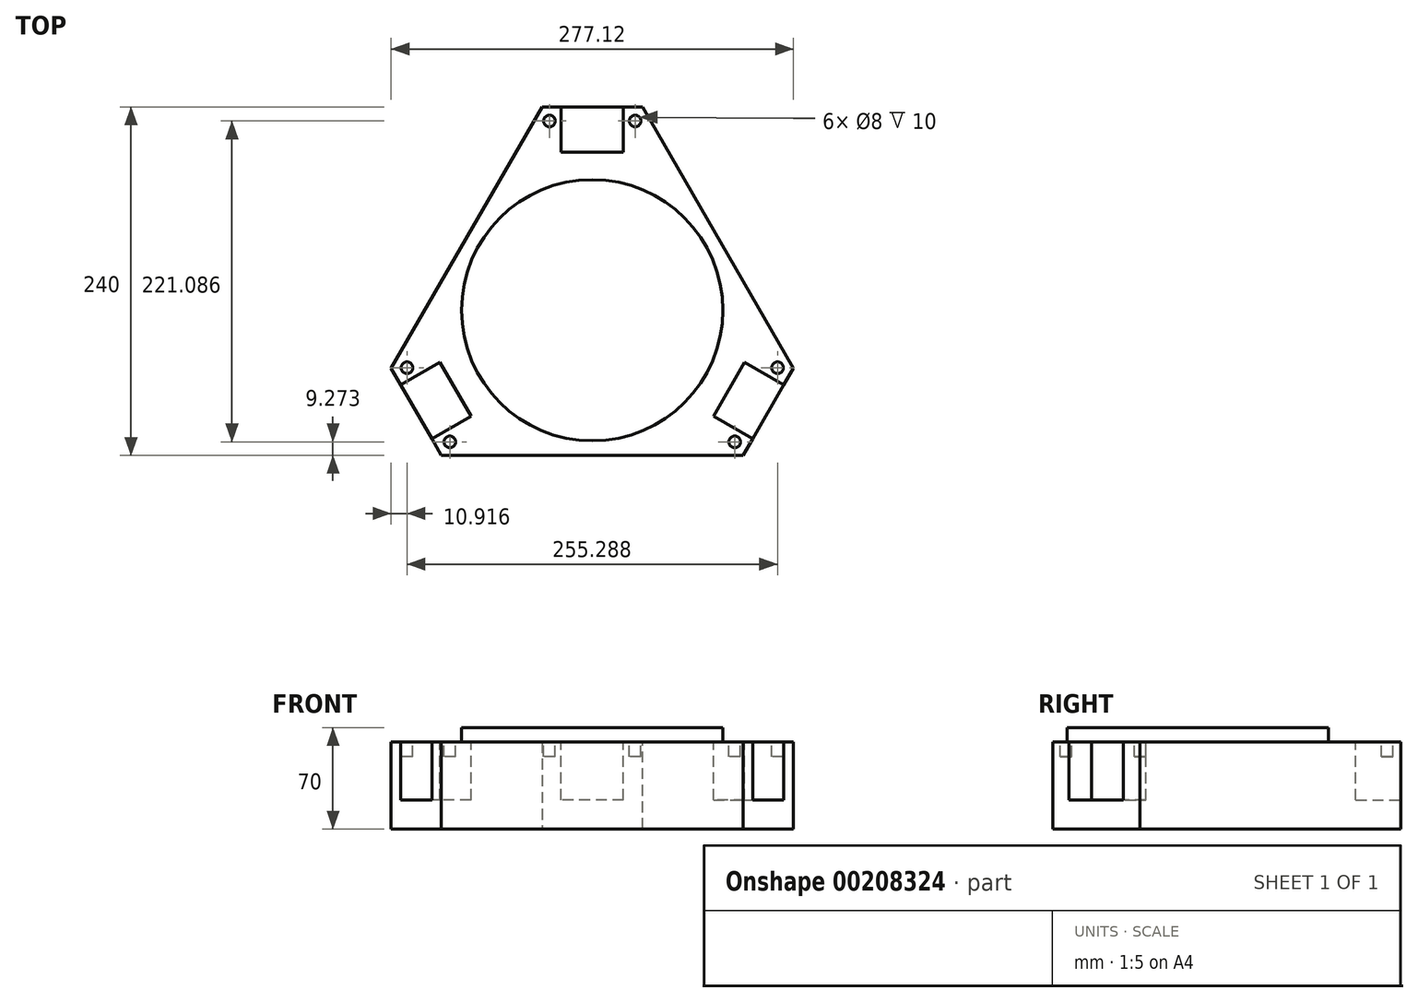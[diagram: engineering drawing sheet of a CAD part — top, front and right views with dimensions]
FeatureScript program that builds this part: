
annotation { "Feature Type Name" : "Feature", "Feature Type Description" : "" }
export const myFeature = defineFeature(function(context is Context, id is Id, definition is map)
    precondition{}
    {
        {
            var Q0;
            Q0=qCreatedBy(makeId("Top.planeOp"),FACE);
            var sketch = newSketch(context, id + "F0", { "sketchPlane" : qUnion([Q0])});
            skCircle(sketch, "E0.cCircle", {"center": v(0, 0) * mm, "radius": 100 * mm, "construction": true});
            skLineSegment(sketch, "E0.0", {"start": v(173.2, -100) * mm, "end": v(-173.2, -100) * mm});
            skLineSegment(sketch, "E0.1", {"start": v(-173.2, -100) * mm, "end": v(0, 200) * mm});
            skLineSegment(sketch, "E0.2", {"start": v(0, 200) * mm, "end": v(173.2, -100) * mm});
            skPoint(sketch, "E0.0.midPoint", {"position": v(0, -100) * mm});
            skSolve(sketch);
        }
        {
            var Q0;
            Q0=qSketchRegion(id+"F0",true);
            extrude(context, id + "F1", {"entities" : qUnion([Q0]), "depth" : 60 * mm});
        }
        {
            var Q0;
            Q0=makeQuery(id+"F1.opExtrude","SWEPT_EDGE",EDGE,{"disambiguationData":[OSD([sQuery(id+"F0.wireOp",EDGE,"E0.0"),sQuery(id+"F0.wireOp",EDGE,"E0.1")])]});
            var Q1;
            Q1=makeQuery(id+"F1.opExtrude","SWEPT_EDGE",EDGE,{"disambiguationData":[OSD([sQuery(id+"F0.wireOp",EDGE,"E0.0"),sQuery(id+"F0.wireOp",EDGE,"E0.2")])]});
            var Q2;
            Q2=makeQuery(id+"F1.opExtrude","SWEPT_EDGE",EDGE,{"disambiguationData":[OSD([sQuery(id+"F0.wireOp",EDGE,"E0.1"),sQuery(id+"F0.wireOp",EDGE,"E0.2")])]});
            chamfer(context, id + "F2", {"entities" : qUnion([Q0, Q1, Q2]), "width" : 40 * mm, "tangentPropagation" : true});
        }
        {
            var Q0;
            Q0=makeQuery(id+"F1.opExtrude","CAP_FACE",FACE,{"disambiguationData":[OSD([sQuery(id+"F0.wireOp",EDGE,"E0.0"),sQuery(id+"F0.wireOp",EDGE,"E0.1"),sQuery(id+"F0.wireOp",EDGE,"E0.2")])],"isStart":false});
            var sketch = newSketch(context, id + "F3", { "sketchPlane" : qUnion([Q0])});
            skCircle(sketch, "E1", {"center": v(0, 0) * mm, "radius": 90 * mm});
            skSolve(sketch);
        }
        {
            var Q0;
            Q0=qSketchRegion(id+"F3",true);
            extrude(context, id + "F4", {"entities" : qUnion([Q0]), "operationType" : NewBodyOperationType.ADD, "depth" : 10 * mm});
        }
        {
            var Q0;
            Q0=makeQuery(id+"F1.opExtrude","CAP_FACE",FACE,{"disambiguationData":[OSD([sQuery(id+"F0.wireOp",EDGE,"E0.0"),sQuery(id+"F0.wireOp",EDGE,"E0.1"),sQuery(id+"F0.wireOp",EDGE,"E0.2")])],"isStart":false});
            var sketch = newSketch(context, id + "F5", { "sketchPlane" : qUnion([Q0])});
            skLineSegment(sketch, "E2.bottom", {"start": v(-21.5, 108.86) * mm, "end": v(21.5, 108.86) * mm});
            skLineSegment(sketch, "E2.top", {"start": v(-21.5, 151.86) * mm, "end": v(21.5, 151.86) * mm});
            skLineSegment(sketch, "E2.left", {"start": v(-21.5, 108.86) * mm, "end": v(-21.5, 151.86) * mm});
            skLineSegment(sketch, "E2.right", {"start": v(21.5, 108.86) * mm, "end": v(21.5, 151.86) * mm});
            skPoint(sketch, "E2.middle", {"position": v(0, 130.36) * mm});
            skLineSegment(sketch, "E3.1.0", {"start": v(-83.52, -73.05) * mm, "end": v(-105.02, -35.8) * mm});
            skPoint(sketch, "E3.1.1", {"position": v(-112.9, -65.18) * mm});
            skLineSegment(sketch, "E3.1.2", {"start": v(-105.02, -35.8) * mm, "end": v(-142.26, -57.3) * mm});
            skLineSegment(sketch, "E3.1.3", {"start": v(-83.52, -73.05) * mm, "end": v(-120.76, -94.55) * mm});
            skLineSegment(sketch, "E3.1.4", {"start": v(-120.76, -94.55) * mm, "end": v(-142.26, -57.3) * mm});
            skLineSegment(sketch, "E3.2.0", {"start": v(105.02, -35.8) * mm, "end": v(83.52, -73.05) * mm});
            skPoint(sketch, "E3.2.1", {"position": v(112.9, -65.18) * mm});
            skLineSegment(sketch, "E3.2.2", {"start": v(83.52, -73.05) * mm, "end": v(120.76, -94.55) * mm});
            skLineSegment(sketch, "E3.2.3", {"start": v(105.02, -35.8) * mm, "end": v(142.26, -57.3) * mm});
            skLineSegment(sketch, "E3.2.4", {"start": v(142.26, -57.3) * mm, "end": v(120.76, -94.55) * mm});
            skPoint(sketch, "E3.center", {"position": v(0, 0) * mm});
            skSolve(sketch);
        }
        {
            var Q0;
            Q0=qSketchRegion(id+"F5",true);
            extrude(context, id + "F6", {"entities" : qUnion([Q0]), "operationType" : NewBodyOperationType.REMOVE, "oppositeDirection" : true, "depth" : 40 * mm});
        }
        {
            var Q0;
            Q0=makeQuery(id+"F1.opExtrude","CAP_FACE",FACE,{"disambiguationData":[OSD([sQuery(id+"F0.wireOp",EDGE,"E0.0"),sQuery(id+"F0.wireOp",EDGE,"E0.1"),sQuery(id+"F0.wireOp",EDGE,"E0.2")])],"isStart":false});
            var sketch = newSketch(context, id + "F7", { "sketchPlane" : qUnion([Q0])});
            skCircle(sketch, "E4", {"center": v(-29.5, 130.36) * mm, "radius": 4 * mm});
            skPoint(sketch, "E4.centerSnap0", {"position": v(-21.5, 130.36) * mm});
            skCircle(sketch, "E5", {"center": v(29.5, 130.36) * mm, "radius": 4 * mm});
            skPoint(sketch, "E5.centerSnap0", {"position": v(21.5, 130.36) * mm});
            skCircle(sketch, "E6.1.0", {"center": v(-98.14, -90.73) * mm, "radius": 4 * mm});
            skCircle(sketch, "E6.1.1", {"center": v(-127.64, -39.63) * mm, "radius": 4 * mm});
            skCircle(sketch, "E6.2.0", {"center": v(127.64, -39.63) * mm, "radius": 4 * mm});
            skCircle(sketch, "E6.2.1", {"center": v(98.14, -90.73) * mm, "radius": 4 * mm});
            skPoint(sketch, "E6.center", {"position": v(0, 0) * mm});
            skSolve(sketch);
        }
        {
            var Q0;
            Q0=qSketchRegion(id+"F7",true);
            extrude(context, id + "F8", {"entities" : qUnion([Q0]), "operationType" : NewBodyOperationType.REMOVE, "oppositeDirection" : true, "depth" : 10 * mm});
        }
    });
